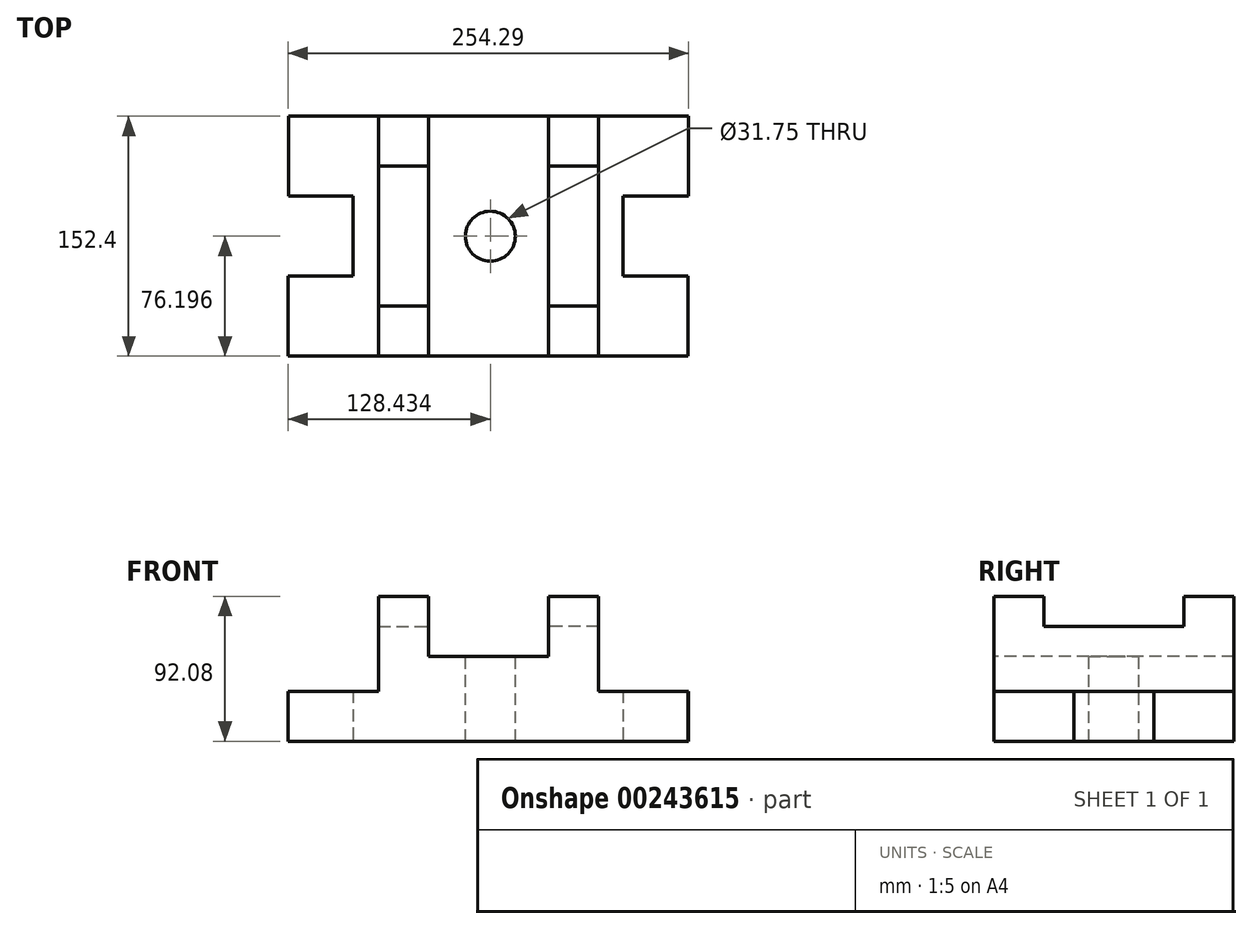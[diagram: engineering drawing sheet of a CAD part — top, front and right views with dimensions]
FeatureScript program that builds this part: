
annotation { "Feature Type Name" : "Feature", "Feature Type Description" : "" }
export const myFeature = defineFeature(function(context is Context, id is Id, definition is map)
    precondition{}
    {
        {
            var Q0;
            Q0=qCreatedBy(makeId("Top.planeOp"),FACE);
            var sketch = newSketch(context, id + "F0", { "sketchPlane" : qUnion([Q0])});
            skLineSegment(sketch, "E0.bottom", {"start": v(-136.28, 73.5) * mm, "end": v(117.72, 73.5) * mm});
            skLineSegment(sketch, "E0.top", {"start": v(-136.28, 22.7) * mm, "end": v(117.72, 22.7) * mm});
            skLineSegment(sketch, "E0.left", {"start": v(-136.28, 73.5) * mm, "end": v(-136.28, 22.7) * mm});
            skLineSegment(sketch, "E0.right", {"start": v(117.72, 73.5) * mm, "end": v(117.72, 22.7) * mm});
            skLineSegment(sketch, "E1.bottom", {"start": v(-136.57, -28.1) * mm, "end": v(117.43, -28.1) * mm});
            skLineSegment(sketch, "E1.top", {"start": v(-136.57, -78.9) * mm, "end": v(117.43, -78.9) * mm});
            skLineSegment(sketch, "E1.left", {"start": v(-136.57, -28.1) * mm, "end": v(-136.57, -78.9) * mm});
            skLineSegment(sketch, "E1.right", {"start": v(117.43, -28.1) * mm, "end": v(117.43, -78.9) * mm});
            skLineSegment(sketch, "E2.bottom", {"start": v(-95.3, 22.7) * mm, "end": v(76.15, 22.7) * mm});
            skLineSegment(sketch, "E2.top", {"start": v(-95.3, -28.1) * mm, "end": v(76.15, -28.1) * mm});
            skLineSegment(sketch, "E2.left", {"start": v(-95.3, 22.7) * mm, "end": v(-95.3, -28.1) * mm});
            skLineSegment(sketch, "E2.right", {"start": v(76.15, 22.7) * mm, "end": v(76.15, -28.1) * mm});
            skSolve(sketch);
        }
        {
            var Q0;
            Q0 = qSketchRegion(id + "F0", true);
            extrude(context, id + "F1", {"entities" : qUnion([Q0]), "depth" : 31.75 * mm});
        }
        {
            var Q0;
            Q0=makeQuery(id+"F1.opExtrude","CAP_FACE",FACE,{"disambiguationData":[OSD([sQuery(id+"F0.wireOp",EDGE,"E0.bottom"),sQuery(id+"F0.wireOp",EDGE,"E0.top"),sQuery(id+"F0.wireOp",EDGE,"E0.left"),sQuery(id+"F0.wireOp",EDGE,"E0.right"),sQuery(id+"F0.wireOp",EDGE,"E1.bottom"),sQuery(id+"F0.wireOp",EDGE,"E1.top"),sQuery(id+"F0.wireOp",EDGE,"E1.left"),sQuery(id+"F0.wireOp",EDGE,"E1.right"),sQuery(id+"F0.wireOp",EDGE,"E2.left"),sQuery(id+"F0.wireOp",EDGE,"E2.right")])],"isStart":false});
            var sketch = newSketch(context, id + "F2", { "sketchPlane" : qUnion([Q0])});
            skLineSegment(sketch, "E3.bottom", {"start": v(-79.13, 73.5) * mm, "end": v(60.57, 73.5) * mm});
            skLineSegment(sketch, "E3.top", {"start": v(-79.13, -78.9) * mm, "end": v(60.57, -78.9) * mm});
            skLineSegment(sketch, "E3.left", {"start": v(-79.13, 73.5) * mm, "end": v(-79.13, -78.9) * mm});
            skLineSegment(sketch, "E3.right", {"start": v(60.57, 73.5) * mm, "end": v(60.57, -78.9) * mm});
            skSolve(sketch);
        }
        {
            var Q0;
            Q0=makeQuery(id+"F2.imprint","IMPRINT",FACE,{"disambiguationData":[TD([[makeQuery(id+"F2.imprint","IMPRINT",EDGE,{"derivedFrom":sQuery(id+"F2.wireOp",EDGE,"E3.bottom")}),-1.0]])]});
            extrude(context, id + "F3", {"entities" : qUnion([Q0]), "operationType" : NewBodyOperationType.ADD, "depth" : 22.22 * mm});
        }
        {
            var Q0;
            Q0=makeQuery(id+"F3.opExtrude","CAP_FACE",FACE,{"disambiguationData":[OSD([sQuery(id+"F2.wireOp",EDGE,"E3.bottom"),sQuery(id+"F2.wireOp",EDGE,"E3.top"),sQuery(id+"F2.wireOp",EDGE,"E3.left"),sQuery(id+"F2.wireOp",EDGE,"E3.right")])],"isStart":false});
            var sketch = newSketch(context, id + "F4", { "sketchPlane" : qUnion([Q0])});
            skLineSegment(sketch, "E4.bottom", {"start": v(-79.13, -78.9) * mm, "end": v(-47.38, -78.9) * mm});
            skLineSegment(sketch, "E4.top", {"start": v(-79.13, -47.14) * mm, "end": v(-47.38, -47.14) * mm});
            skLineSegment(sketch, "E4.left", {"start": v(-79.13, -78.9) * mm, "end": v(-79.13, -47.14) * mm});
            skLineSegment(sketch, "E4.right", {"start": v(-47.38, -78.9) * mm, "end": v(-47.38, -47.14) * mm});
            skLineSegment(sketch, "E5.bottom", {"start": v(-79.13, 73.5) * mm, "end": v(-47.38, 73.5) * mm});
            skLineSegment(sketch, "E5.top", {"start": v(-79.13, 41.76) * mm, "end": v(-47.38, 41.76) * mm});
            skLineSegment(sketch, "E5.left", {"start": v(-79.13, 73.5) * mm, "end": v(-79.13, 41.76) * mm});
            skLineSegment(sketch, "E5.right", {"start": v(-47.38, 73.5) * mm, "end": v(-47.38, 41.76) * mm});
            skLineSegment(sketch, "E6.bottom", {"start": v(60.57, 73.5) * mm, "end": v(28.82, 73.5) * mm});
            skLineSegment(sketch, "E6.top", {"start": v(60.57, 41.76) * mm, "end": v(28.82, 41.76) * mm});
            skLineSegment(sketch, "E6.left", {"start": v(60.57, 73.5) * mm, "end": v(60.57, 41.76) * mm});
            skLineSegment(sketch, "E6.right", {"start": v(28.82, 73.5) * mm, "end": v(28.82, 41.76) * mm});
            skLineSegment(sketch, "E7.bottom", {"start": v(60.57, -78.9) * mm, "end": v(28.82, -78.9) * mm});
            skLineSegment(sketch, "E7.top", {"start": v(60.57, -47.14) * mm, "end": v(28.82, -47.14) * mm});
            skLineSegment(sketch, "E7.left", {"start": v(60.57, -78.9) * mm, "end": v(60.57, -47.14) * mm});
            skLineSegment(sketch, "E7.right", {"start": v(28.82, -78.9) * mm, "end": v(28.82, -47.14) * mm});
            skSolve(sketch);
        }
        {
            var Q0;
            Q0=makeQuery(id+"F4.imprint","IMPRINT",FACE,{"disambiguationData":[TD([[makeQuery(id+"F4.imprint","IMPRINT",EDGE,{"derivedFrom":sQuery(id+"F4.wireOp",EDGE,"E5.bottom")}),-1.0]])]});
            var Q1;
            Q1=makeQuery(id+"F4.imprint","IMPRINT",FACE,{"disambiguationData":[TD([[makeQuery(id+"F4.imprint","IMPRINT",EDGE,{"derivedFrom":sQuery(id+"F4.wireOp",EDGE,"E4.bottom")}),1.0]])]});
            var Q2;
            Q2=makeQuery(id+"F4.imprint","IMPRINT",FACE,{"disambiguationData":[TD([[makeQuery(id+"F4.imprint","IMPRINT",EDGE,{"derivedFrom":sQuery(id+"F4.wireOp",EDGE,"E7.bottom")}),1.0]])]});
            var Q3;
            Q3=makeQuery(id+"F4.imprint","IMPRINT",FACE,{"disambiguationData":[TD([[makeQuery(id+"F4.imprint","IMPRINT",EDGE,{"derivedFrom":sQuery(id+"F4.wireOp",EDGE,"E6.bottom")}),-1.0]])]});
            extrude(context, id + "F5", {"entities" : qUnion([Q0, Q1, Q2, Q3]), "operationType" : NewBodyOperationType.ADD, "depth" : 38.1 * mm});
        }
        {
            var Q0;
            Q0=makeQuery(id+"F3.opExtrude","CAP_FACE",FACE,{"disambiguationData":[OSD([sQuery(id+"F2.wireOp",EDGE,"E3.bottom"),sQuery(id+"F2.wireOp",EDGE,"E3.top"),sQuery(id+"F2.wireOp",EDGE,"E3.left"),sQuery(id+"F2.wireOp",EDGE,"E3.right")])],"isStart":false});
            var sketch = newSketch(context, id + "F6", { "sketchPlane" : qUnion([Q0])});
            skLineSegment(sketch, "E8.bottom", {"start": v(-79.13, 41.76) * mm, "end": v(-47.38, 41.76) * mm});
            skLineSegment(sketch, "E8.top", {"start": v(-79.13, -47.14) * mm, "end": v(-47.38, -47.14) * mm});
            skLineSegment(sketch, "E8.left", {"start": v(-79.13, 41.76) * mm, "end": v(-79.13, -47.14) * mm});
            skLineSegment(sketch, "E8.right", {"start": v(-47.38, 41.76) * mm, "end": v(-47.38, -47.14) * mm});
            skLineSegment(sketch, "E9.bottom", {"start": v(28.82, 41.76) * mm, "end": v(60.57, 41.76) * mm});
            skLineSegment(sketch, "E9.top", {"start": v(28.82, -47.14) * mm, "end": v(60.57, -47.14) * mm});
            skLineSegment(sketch, "E9.left", {"start": v(28.82, 41.76) * mm, "end": v(28.82, -47.14) * mm});
            skLineSegment(sketch, "E9.right", {"start": v(60.57, 41.76) * mm, "end": v(60.57, -47.14) * mm});
            skSolve(sketch);
        }
        {
            var Q0;
            Q0=makeQuery(id+"F6.imprint","IMPRINT",FACE,{"disambiguationData":[TD([[makeQuery(id+"F6.imprint","IMPRINT",EDGE,{"derivedFrom":sQuery(id+"F6.wireOp",EDGE,"E8.bottom")}),-1.0]])]});
            var Q1;
            Q1=makeQuery(id+"F6.imprint","IMPRINT",FACE,{"disambiguationData":[TD([[makeQuery(id+"F6.imprint","IMPRINT",EDGE,{"derivedFrom":sQuery(id+"F6.wireOp",EDGE,"E9.bottom")}),1.0]])]});
            extrude(context, id + "F7", {"entities" : qUnion([Q0, Q1]), "operationType" : NewBodyOperationType.ADD, "depth" : 19.05 * mm});
        }
        {
            var Q0;
            Q0=makeQuery(id+"F3.opExtrude","CAP_FACE",FACE,{"disambiguationData":[OSD([sQuery(id+"F2.wireOp",EDGE,"E3.bottom"),sQuery(id+"F2.wireOp",EDGE,"E3.top"),sQuery(id+"F2.wireOp",EDGE,"E3.left"),sQuery(id+"F2.wireOp",EDGE,"E3.right")])],"isStart":false});
            var sketch = newSketch(context, id + "F8", { "sketchPlane" : qUnion([Q0])});
            skCircle(sketch, "E10", {"center": v(-8.14, -2.7) * mm, "radius": 15.88 * mm});
            skSolve(sketch);
        }
        {
            var Q0;
            Q0=sQuery(id+"F8.wireOp",VERTEX,"E10.center");
            var Q1;
            Q1=makeQuery(id+"F1.opExtrude","SWEPT_BODY",BODY,{"disambiguationData":[OSD([sQuery(id+"F0.wireOp",EDGE,"E0.bottom"),sQuery(id+"F0.wireOp",EDGE,"E0.top"),sQuery(id+"F0.wireOp",EDGE,"E0.left"),sQuery(id+"F0.wireOp",EDGE,"E0.right"),sQuery(id+"F0.wireOp",EDGE,"E1.bottom"),sQuery(id+"F0.wireOp",EDGE,"E1.top"),sQuery(id+"F0.wireOp",EDGE,"E1.left"),sQuery(id+"F0.wireOp",EDGE,"E1.right"),sQuery(id+"F0.wireOp",EDGE,"E2.left"),sQuery(id+"F0.wireOp",EDGE,"E2.right")])]});
            hole(context, id + "F9", {"style" : HoleStyle.SIMPLE, "endStyle" : HoleEndStyle.THROUGH, "holeDiameter" : 31.75 * mm, "locations" : qUnion([Q0]), "scope" : qUnion([Q1]), "isTappedThrough" : true});
        }
    });
